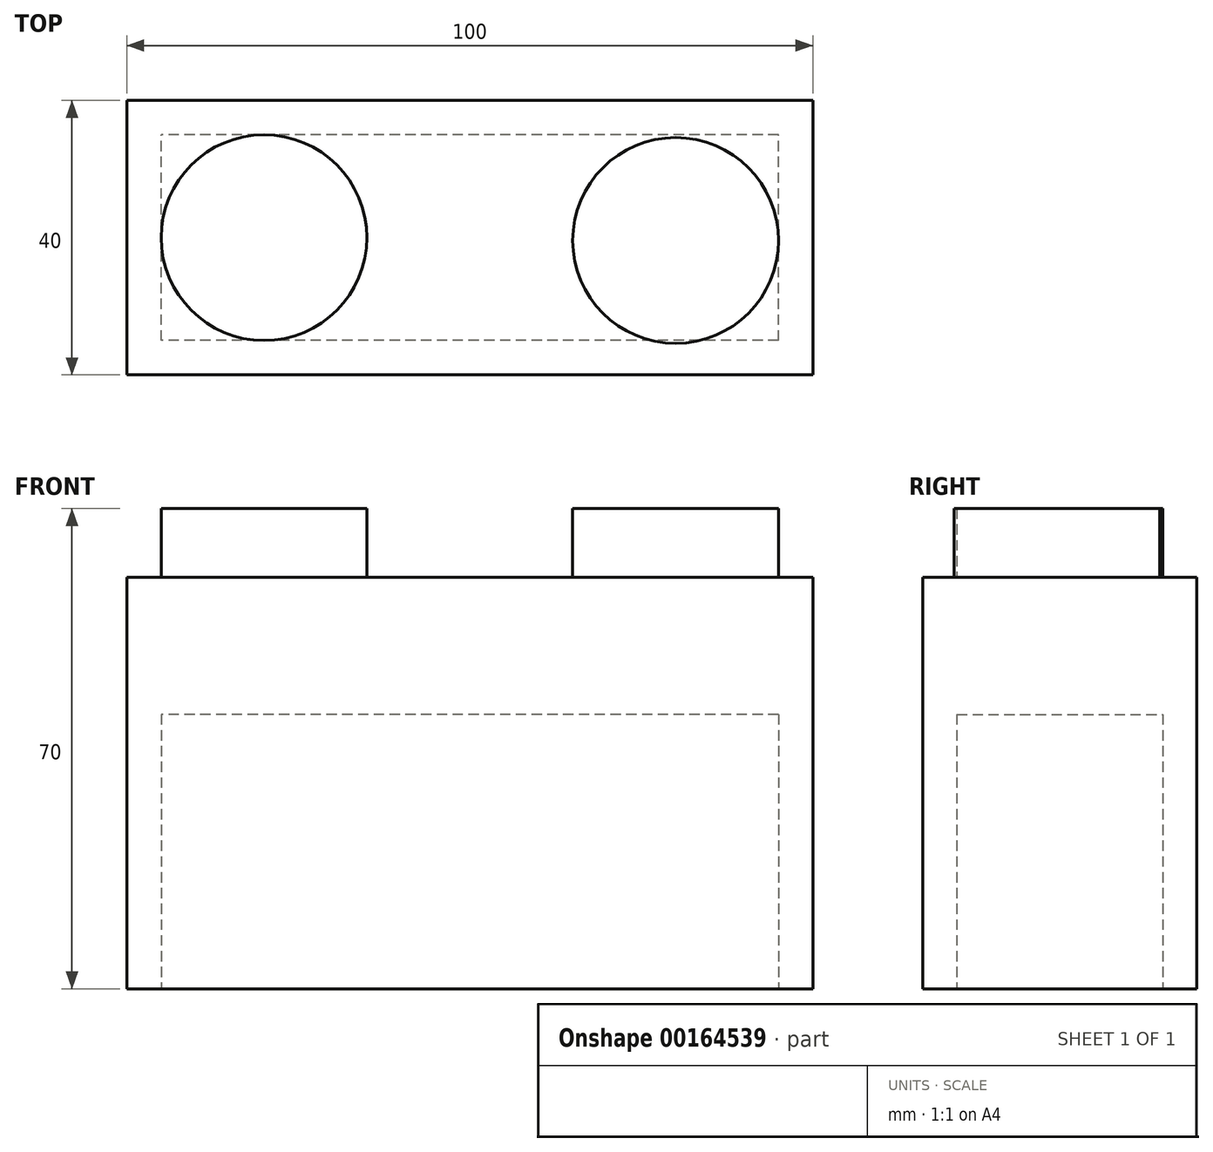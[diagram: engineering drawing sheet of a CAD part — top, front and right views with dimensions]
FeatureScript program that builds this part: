
annotation { "Feature Type Name" : "Feature", "Feature Type Description" : "" }
export const myFeature = defineFeature(function(context is Context, id is Id, definition is map)
    precondition{}
    {
        {
            var Q0;
            Q0=qCreatedBy(makeId("Front.planeOp"),FACE);
            var sketch = newSketch(context, id + "F0", { "sketchPlane" : qUnion([Q0])});
            skLineSegment(sketch, "E0.bottom", {"start": v(50, 30) * mm, "end": v(-50, 30) * mm});
            skLineSegment(sketch, "E0.top", {"start": v(50, -30) * mm, "end": v(-50, -30) * mm});
            skLineSegment(sketch, "E0.left", {"start": v(50, 30) * mm, "end": v(50, -30) * mm});
            skLineSegment(sketch, "E0.right", {"start": v(-50, 30) * mm, "end": v(-50, -30) * mm});
            skPoint(sketch, "E0.middle", {"position": v(0, 0) * mm});
            skSolve(sketch);
        }
        {
            var Q0;
            Q0=makeQuery(id+"F0.imprint","IMPRINT",FACE,{"disambiguationData":[TD([[makeQuery(id+"F0.imprint","IMPRINT",EDGE,{"derivedFrom":sQuery(id+"F0.wireOp",EDGE,"E0.bottom")}),1.0]])]});
            extrude(context, id + "F1", {"entities" : qUnion([Q0]), "depth" : 40 * mm});
        }
        {
            var Q0;
            Q0=makeQuery(id+"F1.opExtrude","SWEPT_FACE",FACE,{"disambiguationData":[OSD([sQuery(id+"F0.wireOp",EDGE,"E0.bottom")])]});
            var sketch = newSketch(context, id + "F2", { "sketchPlane" : qUnion([Q0])});
            skSolve(sketch);
        }
        {
            var Q0;
            {var subQ0=sQuery(id+"F0.wireOp",EDGE,"E0.bottom");Q0=makeQuery(id+"F2.imprint","IMPRINT",FACE,{"disambiguationData":[TD([[makeQuery(id+"F2.imprint","IMPRINT",EDGE,{"derivedFrom":makeQuery(id+"F1.opExtrude","CAP_EDGE",EDGE,{"disambiguationData":[OSD([subQ0])],"isStart":true})}),1.0]])]});}
            var sketch = newSketch(context, id + "F3", { "sketchPlane" : qUnion([Q0])});
            skCircle(sketch, "E1", {"center": v(-30, -20) * mm, "radius": 15 * mm});
            skCircle(sketch, "E2", {"center": v(30, -20.41) * mm, "radius": 15 * mm});
            skSolve(sketch);
        }
        {
            var Q0;
            Q0 = qSketchRegion(id + "F3", true);
            extrude(context, id + "F4", {"entities" : qUnion([Q0]), "operationType" : NewBodyOperationType.ADD, "depth" : 10 * mm});
        }
        {
            var Q0;
            Q0=makeQuery(id+"F1.opExtrude","SWEPT_FACE",FACE,{"disambiguationData":[OSD([sQuery(id+"F0.wireOp",EDGE,"E0.top")])]});
            var sketch = newSketch(context, id + "F5", { "sketchPlane" : qUnion([Q0])});
            skLineSegment(sketch, "E3.bottom", {"start": v(45, 35) * mm, "end": v(-45, 35) * mm});
            skLineSegment(sketch, "E3.top", {"start": v(45, 5) * mm, "end": v(-45, 5) * mm});
            skLineSegment(sketch, "E3.left", {"start": v(45, 35) * mm, "end": v(45, 5) * mm});
            skLineSegment(sketch, "E3.right", {"start": v(-45, 35) * mm, "end": v(-45, 5) * mm});
            skPoint(sketch, "E3.middle", {"position": v(0, 20) * mm});
            skPoint(sketch, "E3.middle.positionSnap0", {"position": v(50, 20) * mm});
            skPoint(sketch, "E3.centerSnap0", {"position": v(50, 20) * mm});
            skSolve(sketch);
        }
        {
            var Q0;
            Q0 = qSketchRegion(id + "F5", true);
            extrude(context, id + "F6", {"entities" : qUnion([Q0]), "operationType" : NewBodyOperationType.REMOVE, "oppositeDirection" : true, "depth" : 40 * mm});
        }
    });
